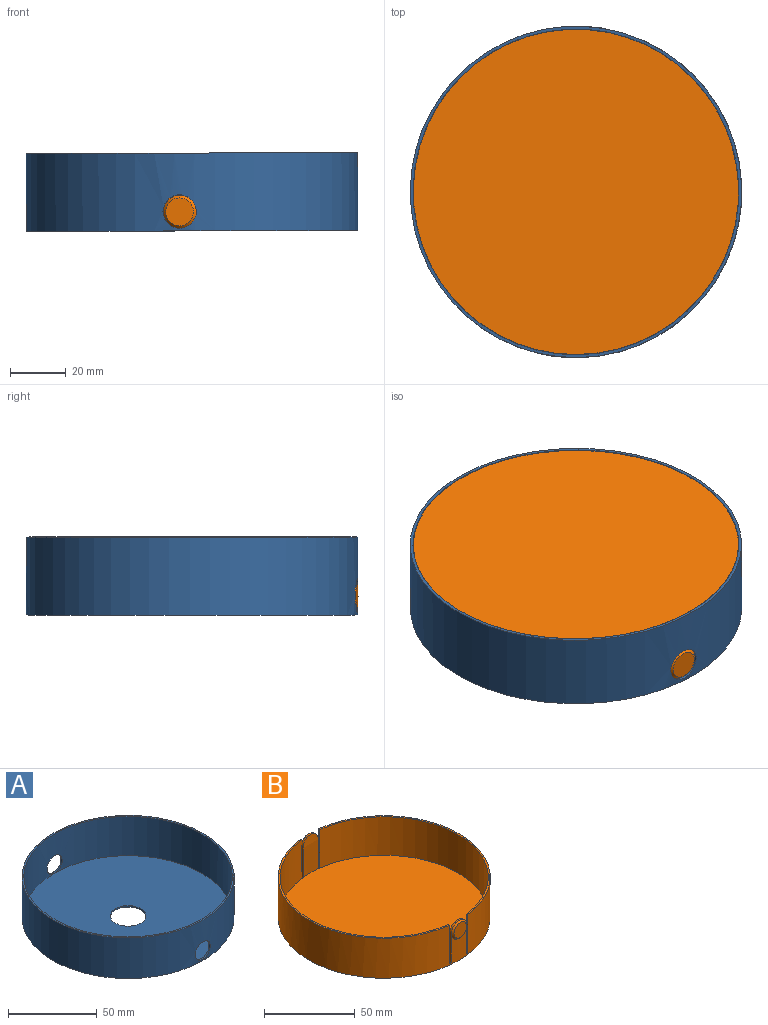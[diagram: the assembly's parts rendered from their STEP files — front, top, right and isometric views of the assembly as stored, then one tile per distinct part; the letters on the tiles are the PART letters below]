
ASSEMBLY  parts=2 mates=1
PART A: 8 faces, bbox 119.2x119.2x28 mm
  f0: cylinder r=59.6mm len=119.2mm, axis (0,0,-1), area 10258.1mm2, adj f1,f2,f6,f7
  f1: plane 119.2x119.2mm, normal (0,0,1), area 371.3mm2, adj f0,f3
  f2: plane 119.2x119.2mm, normal (0,0,-1), area 10845.3mm2, adj f0,f5
  f3: cylinder r=58.6mm len=117.2mm, axis (0,0,-1), area 9714.3mm2, adj f1,f4,f6,f7
  f4: plane 117.2x117.2mm, normal (0,0,1), area 10473.9mm2, adj f3,f5
  f5: cylinder r=10mm len=20mm, axis (0,0,-1), area 62.8mm2, adj f2,f4
  f6: cylinder r=6mm len=12mm, axis (0,-1,0), area 37.8mm2, adj f0,f3
  f7: cylinder r=6mm len=12mm, axis (0,-1,0), area 37.8mm2, adj f0,f3
PART B: 27 faces, bbox 117x119x27 mm
  f0: cylinder r=58.5mm len=117mm, axis (0,0,-1), area 9562.6mm2, adj f3,f6,f7,f9,f10,f11,f12,f13
  f1: cylinder r=57.5mm len=26mm, axis (0,0,-1), area 297.2mm2, adj f8,f12,f13,f18,f21,f22
  f2: cylinder r=57.5mm len=26mm, axis (0,0,-1), area 297.2mm2, adj f8,f10,f11,f15,f19,f20
  f3: plane 116.16x51.5mm, normal (0,0,1), area 168.2mm2, adj f0,f5,f9,f14
  f4: cylinder r=57.5mm len=114.26mm, axis (0,0,-1), area 4331.9mm2, adj f6,f8,f16,f17,f19,f21
  f5: cylinder r=57.5mm len=114.26mm, axis (0,0,-1), area 4331.9mm2, adj f3,f8,f9,f14,f20,f22
  f6: plane 116.16x51.5mm, normal (0,0,1), area 168.2mm2, adj f0,f4,f16,f17
  f7: plane 117x117mm, normal (0,0,-1), area 10751.3mm2, adj f0
  f8: plane 115x115mm, normal (0,0,1), area 10386.9mm2, adj f1,f2,f4,f5
  f9: plane 25.5x1.01mm, normal (-1,0,0), area 25.7mm2, adj f0,f3,f5,f20
  f10: plane 19.5x1.01mm, normal (1,0,0), area 19.6mm2, adj f0,f2,f11,f20
  f11: cylinder r=6mm len=12mm, axis (0,-1,0), area 24.7mm2, adj f0,f2,f10,f15,f25
  f12: cylinder r=6mm len=12mm, axis (0,-1,0), area 24.7mm2, adj f0,f1,f13,f18,f26
  f13: plane 19.5x1.01mm, normal (1,0,0), area 19.6mm2, adj f0,f1,f12,f22
  f14: plane 25.5x1.01mm, normal (-1,0,0), area 25.7mm2, adj f0,f3,f5,f22
  f15: plane 19.5x1.01mm, normal (-1,0,0), area 19.6mm2, adj f0,f2,f11,f19
  f16: plane 25.5x1.01mm, normal (1,0,0), area 25.7mm2, adj f0,f4,f6,f19
  f17: plane 25.5x1.01mm, normal (1,0,0), area 25.7mm2, adj f0,f4,f6,f21
  f18: plane 19.5x1.01mm, normal (-1,0,0), area 19.6mm2, adj f0,f1,f12,f21
  f19: cylinder r=0.5mm len=1.12mm, axis (0,1,0), area 1.6mm2, adj f0,f2,f4,f15,f16
  f20: cylinder r=0.5mm len=1.12mm, axis (0,1,0), area 1.6mm2, adj f0,f2,f5,f9,f10
  f21: cylinder r=0.5mm len=1.12mm, axis (0,1,0), area 1.6mm2, adj f0,f1,f4,f17,f18
  f22: cylinder r=0.5mm len=1.12mm, axis (0,1,0), area 1.6mm2, adj f0,f1,f5,f13,f14
  f23: plane 10x10mm, normal (0,-1,0), area 78.5mm2, adj f25
  f24: plane 10x10mm, normal (0,1,0), area 78.5mm2, adj f26
  f25: cone r=5mm half-angle=45deg, axis (0,1,0), area 48.9mm2, adj f11,f23
  f26: cone r=6mm half-angle=45deg, axis (0,-1,0), area 48.9mm2, adj f12,f24
PLACE A rot(axis=(0,-0.04,-1),4.4deg) t=(11.06,56.6,60.14)mm
PLACE B rot(axis=(1,-0.04,0),180deg) t=(10.97,56.61,88)mm
MATE slider A.f0 <-> B.f0  axis (0,0,-1) through (11.01,56.61,74.64)mm
